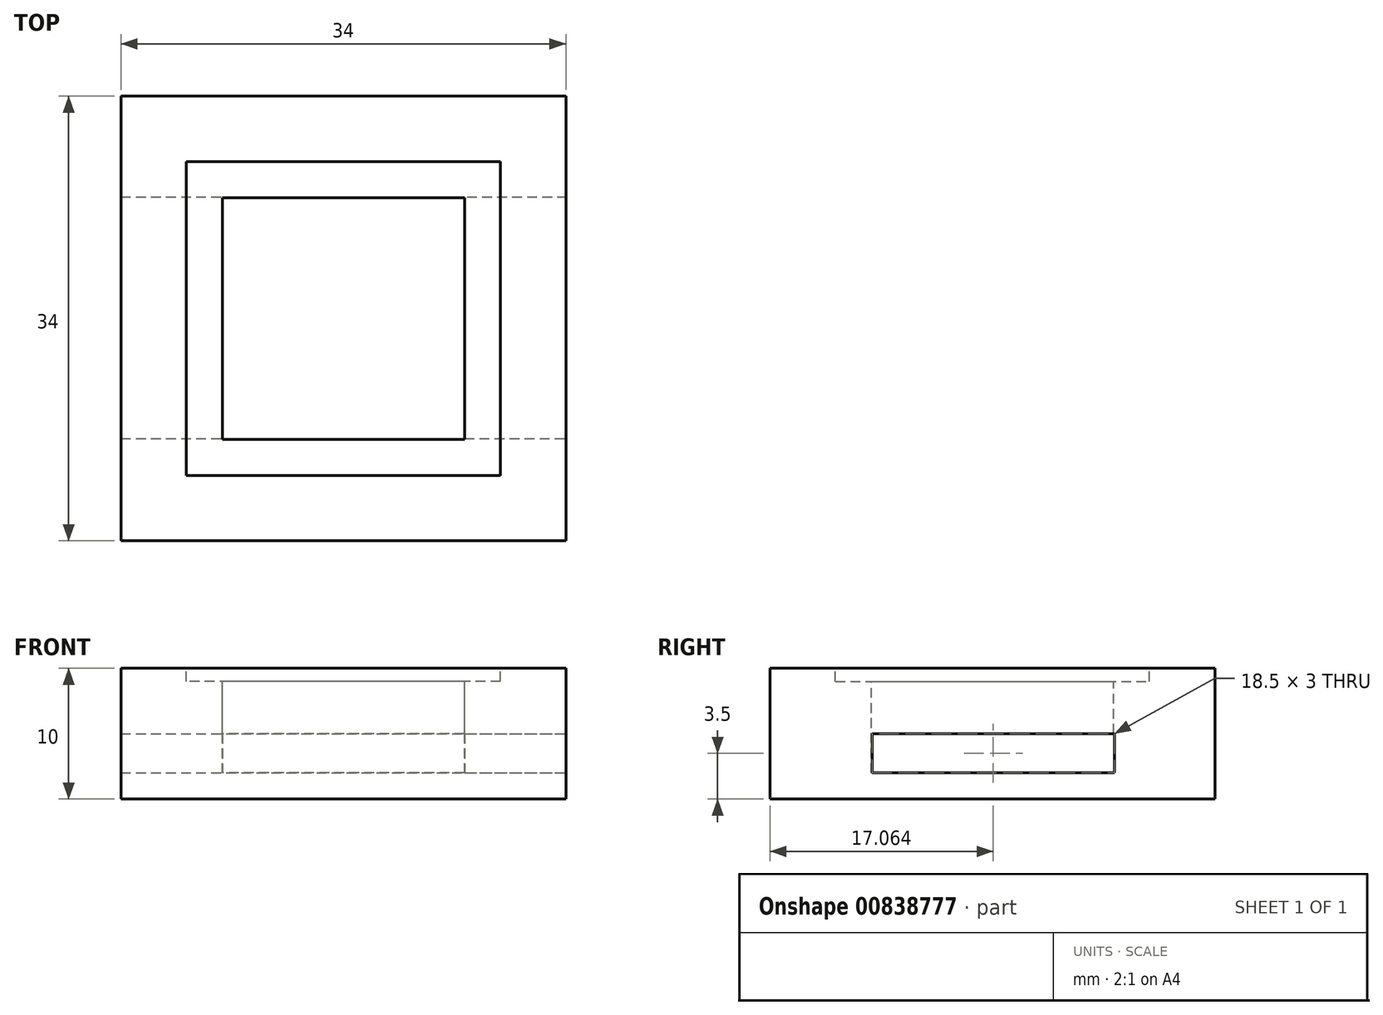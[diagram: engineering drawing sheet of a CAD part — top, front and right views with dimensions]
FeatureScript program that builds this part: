
annotation { "Feature Type Name" : "Feature", "Feature Type Description" : "" }
export const myFeature = defineFeature(function(context is Context, id is Id, definition is map)
    precondition{}
    {
        {
            var Q0;
            Q0=qCreatedBy(makeId("Top.planeOp"),FACE);
            var sketch = newSketch(context, id + "F0", { "sketchPlane" : qUnion([Q0])});
            skLineSegment(sketch, "E0.bottom", {"start": v(9.25, -9.25) * mm, "end": v(-9.25, -9.25) * mm});
            skLineSegment(sketch, "E0.top", {"start": v(9.25, 9.25) * mm, "end": v(-9.25, 9.25) * mm});
            skLineSegment(sketch, "E0.left", {"start": v(9.25, -9.25) * mm, "end": v(9.25, 9.25) * mm});
            skLineSegment(sketch, "E0.right", {"start": v(-9.25, -9.25) * mm, "end": v(-9.25, 9.25) * mm});
            skPoint(sketch, "E0.middle", {"position": v(0, 0) * mm});
            skSolve(sketch);
        }
        {
            var Q0;
            Q0=qCreatedBy(makeId("Top.planeOp"),FACE);
            var sketch = newSketch(context, id + "F1", { "sketchPlane" : qUnion([Q0])});
            skLineSegment(sketch, "E1.bottom", {"start": v(12, -12) * mm, "end": v(-12, -12) * mm});
            skLineSegment(sketch, "E1.top", {"start": v(12, 12) * mm, "end": v(-12, 12) * mm});
            skLineSegment(sketch, "E1.left", {"start": v(12, -12) * mm, "end": v(12, 12) * mm});
            skLineSegment(sketch, "E1.right", {"start": v(-12, -12) * mm, "end": v(-12, 12) * mm});
            skPoint(sketch, "E1.middle", {"position": v(0, 0) * mm});
            skSolve(sketch);
        }
        {
            var Q0;
            Q0=qCreatedBy(makeId("Top.planeOp"),FACE);
            var sketch = newSketch(context, id + "F2", { "sketchPlane" : qUnion([Q0])});
            skLineSegment(sketch, "E2.bottom", {"start": v(17, -17) * mm, "end": v(-17, -17) * mm});
            skLineSegment(sketch, "E2.top", {"start": v(17, 17) * mm, "end": v(-17, 17) * mm});
            skLineSegment(sketch, "E2.left", {"start": v(17, -17) * mm, "end": v(17, 17) * mm});
            skLineSegment(sketch, "E2.right", {"start": v(-17, -17) * mm, "end": v(-17, 17) * mm});
            skPoint(sketch, "E2.middle", {"position": v(0, 0) * mm});
            skSolve(sketch);
        }
        {
            var Q0;
            Q0=qSketchRegion(id+"F2",true);
            extrude(context, id + "F3", {"entities" : qUnion([Q0]), "oppositeDirection" : true, "depth" : 10 * mm, "offsetDistance" : 25 * mm});
        }
        {
            var Q0;
            Q0=qSketchRegion(id+"F1",true);
            extrude(context, id + "F4", {"entities" : qUnion([Q0]), "operationType" : NewBodyOperationType.REMOVE, "oppositeDirection" : true, "depth" : 1 * mm, "offsetDistance" : 25 * mm});
        }
        {
            var Q0;
            Q0=qSketchRegion(id+"F0",true);
            extrude(context, id + "F5", {"entities" : qUnion([Q0]), "operationType" : NewBodyOperationType.REMOVE, "oppositeDirection" : true, "depth" : 8 * mm, "offsetDistance" : 25 * mm});
        }
        {
            var Q0;
            Q0=makeQuery(id+"F3.opExtrude","SWEPT_FACE",FACE,{"disambiguationData":[OSD([sQuery(id+"F2.wireOp",EDGE,"E2.left")])]});
            var sketch = newSketch(context, id + "F6", { "sketchPlane" : qUnion([Q0])});
            skLineSegment(sketch, "E3.bottom", {"start": v(-9.19, -5) * mm, "end": v(9.31, -5) * mm});
            skLineSegment(sketch, "E3.top", {"start": v(-9.19, -8) * mm, "end": v(9.31, -8) * mm});
            skLineSegment(sketch, "E3.left", {"start": v(-9.19, -5) * mm, "end": v(-9.19, -8) * mm});
            skLineSegment(sketch, "E3.right", {"start": v(9.31, -5) * mm, "end": v(9.31, -8) * mm});
            skSolve(sketch);
        }
        {
            var Q0;
            Q0=qSketchRegion(id+"F6",true);
            extrude(context, id + "F7", {"entities" : qUnion([Q0]), "operationType" : NewBodyOperationType.REMOVE, "oppositeDirection" : true, "depth" : 34 * mm, "offsetDistance" : 25 * mm});
        }
    });
